MODEL slx_2e647110513d
CONFIG AbsTol = auto
CONFIG FixedStep = 0.001
CONFIG MaxStep = auto
CONFIG MinStep = auto
CONFIG RelTol = 1e-3
CONFIG SampleTimeConstraint = Unconstrained
CONFIG Solver = ode5
CONFIG SolverMode = Auto
CONFIG SolverName = ode5
CONFIG StartTime = 0.0
CONFIG StopTime = 15
BLOCK [SubSystem] Control Block
  Ports = [5, 1]
  RequestExecContextInheritance = off
BLOCK [Fcn] Control Block/Fcn
  Expr = cos(u)
BLOCK [Fcn] Control Block/Fcn1
  Expr = sin(u)/u
BLOCK [Gain] Control Block/Gain
  Gain = Kx
  OutDataTypeStr = Inherit: Inherit via internal rule
  ParamDataTypeStr = Inherit: Inherit via internal rule
  SaturateOnIntegerOverflow = off
BLOCK [Gain] Control Block/Gain1
  Gain = Ky
  OutDataTypeStr = Inherit: Inherit via internal rule
  ParamDataTypeStr = Inherit: Inherit via internal rule
  SaturateOnIntegerOverflow = off
BLOCK [Gain] Control Block/Gain2
  Gain = Kt
  OutDataTypeStr = Inherit: Inherit via internal rule
  ParamDataTypeStr = Inherit: Inherit via internal rule
  SaturateOnIntegerOverflow = off
BLOCK [Mux] Control Block/Mux
  DisplayOption = bar
  Inputs = 2
  Ports = [2, 1]
BLOCK [Mux] Control Block/Mux1
  DisplayOption = bar
  Inputs = 3
  Ports = [3, 1]
BLOCK [Product] Control Block/Product
  InputSameDT = off
  Inputs = 3
  OutDataTypeStr = Inherit: Inherit via internal rule
  Ports = [3, 1]
  RndMeth = Floor
  SaturateOnIntegerOverflow = off
BLOCK [Sum] Control Block/Sum3
  IconShape = round
  InputSameDT = off
  Inputs = |++
  OutDataTypeStr = Inherit: Inherit via internal rule
  Ports = [2, 1]
  SaturateOnIntegerOverflow = off
BLOCK [Sum] Control Block/Sum4
  IconShape = round
  InputSameDT = off
  Inputs = +++
  OutDataTypeStr = Inherit: Inherit via internal rule
  Ports = [3, 1]
  SaturateOnIntegerOverflow = off
BLOCK [ToWorkspace] Control Block/To Workspace
  FixptAsFi = on
  MaxDataPoints = inf
  Ports = [1]
  SampleTime = -1
  Save2DSignal = 3-D array (concatenate along third dimension)
  VariableName = error
BLOCK [Inport] Control Block/V_ref
  IconDisplay = Port number
  Port = 4
BLOCK [Inport] Control Block/theta_e
  IconDisplay = Port number
  Port = 3
BLOCK [Inport] Control Block/theta_ref
  IconDisplay = Port number
  Port = 5
BLOCK [Outport] Control Block/u_m
  IconDisplay = Port number
BLOCK [Inport] Control Block/x_e
  IconDisplay = Port number
BLOCK [Inport] Control Block/y_e
  IconDisplay = Port number
  Port = 2
BLOCK [SubSystem] DKM
  Ports = [1, 1]
  RequestExecContextInheritance = off
BLOCK [Constant] DKM/F_inv
  Value = [r/2 r/2; r/(2*L) -r/(2*L)]
BLOCK [ToWorkspace] DKM/To Workspace
  FixptAsFi = on
  MaxDataPoints = inf
  Ports = [1]
  SampleTime = -1
  Save2DSignal = 3-D array (concatenate along third dimension)
  VariableName = u
BLOCK [Inport] DKM/qm_dot
  IconDisplay = Port number
BLOCK [Outport] DKM/u_m 
  IconDisplay = Port number
BLOCK [Product] DKM/u_m Func
  InputSameDT = off
  Multiplication = Matrix(*)
  OutDataTypeStr = Inherit: Inherit via internal rule
  Ports = [2, 1]
  RndMeth = Floor
  SaturateOnIntegerOverflow = off
BLOCK [Gain] IKM
  Gain = [1/r_e L_e/r_e; 1/r_e  -L_e/r_e]
  Multiplication = Matrix(K*u) (u vector)
  OutDataTypeStr = Inherit: Inherit via internal rule
  ParamDataTypeStr = Inherit: Inherit via internal rule
  SaturateOnIntegerOverflow = off
BLOCK [SubSystem] Localization
  Ports = [1, 3]
  RequestExecContextInheritance = off
BLOCK [Demux] Localization/Demux
  DisplayOption = bar
  Outputs = 2
  Ports = [1, 2]
BLOCK [Fcn] Localization/Fcn
  Expr = cos(u)
BLOCK [Fcn] Localization/Fcn1
  Expr = sin(u)
BLOCK [Integrator] Localization/Integrator
  InitialCondition = theta0
  Ports = [1, 1]
BLOCK [Integrator] Localization/Integrator1
  InitialCondition = x0
  Ports = [1, 1]
BLOCK [Integrator] Localization/Integrator2
  InitialCondition = y0
  Ports = [1, 1]
BLOCK [Mux] Localization/Mux1
  DisplayOption = bar
  Inputs = 3
  Ports = [3, 1]
BLOCK [Product] Localization/Product
  InputSameDT = off
  OutDataTypeStr = Inherit: Inherit via internal rule
  Ports = [2, 1]
  RndMeth = Floor
  SaturateOnIntegerOverflow = off
BLOCK [Product] Localization/Product1
  InputSameDT = off
  OutDataTypeStr = Inherit: Inherit via internal rule
  Ports = [2, 1]
  RndMeth = Floor
  SaturateOnIntegerOverflow = off
BLOCK [ToWorkspace] Localization/To Workspace
  FixptAsFi = on
  MaxDataPoints = inf
  Ports = [1]
  SampleTime = -1
  Save2DSignal = 3-D array (concatenate along third dimension)
  VariableName = h
BLOCK [SubSystem] Localization/Transformation
  Ports = [3, 2]
  RequestExecContextInheritance = off
BLOCK [Inport] Localization/Transformation/0x
  IconDisplay = Port number
  Port = 2
BLOCK [Inport] Localization/Transformation/0y
  IconDisplay = Port number
  Port = 3
BLOCK [Demux] Localization/Transformation/Demux
  DisplayOption = bar
  Outputs = 2
  Ports = [1, 2]
BLOCK [Fcn] Localization/Transformation/Fcn2
  Expr = cos(u)
BLOCK [Fcn] Localization/Transformation/Fcn3
  Expr = sin(u)
BLOCK [Gain] Localization/Transformation/Gain
  Gain = -1
  OutDataTypeStr = Inherit: Inherit via internal rule
  ParamDataTypeStr = Inherit: Inherit via internal rule
  SaturateOnIntegerOverflow = off
BLOCK [Concatenate] Localization/Transformation/Matrix Concatenate
  ConcatenateDimension = 2
  Mode = Multidimensional array
  Ports = [2, 1]
BLOCK [Mux] Localization/Transformation/Mux1
  DisplayOption = bar
  Inputs = 2
  Ports = [2, 1]
BLOCK [Mux] Localization/Transformation/Mux2
  DisplayOption = bar
  Inputs = 2
  Ports = [2, 1]
BLOCK [Mux] Localization/Transformation/Mux3
  DisplayOption = bar
  Inputs = 2
  Ports = [2, 1]
BLOCK [Product] Localization/Transformation/Product
  InputSameDT = off
  Multiplication = Matrix(*)
  OutDataTypeStr = Inherit: Inherit via internal rule
  Ports = [2, 1]
  RndMeth = Floor
  SaturateOnIntegerOverflow = off
BLOCK [Outport] Localization/Transformation/mx
  IconDisplay = Port number
BLOCK [Outport] Localization/Transformation/my
  IconDisplay = Port number
  Port = 2
BLOCK [Inport] Localization/Transformation/theta
  IconDisplay = Port number
BLOCK [Outport] Localization/theta
  IconDisplay = Port number
  Port = 3
BLOCK [Inport] Localization/u_m
  IconDisplay = Port number
BLOCK [Outport] Localization/x
  IconDisplay = Port number
BLOCK [Outport] Localization/y
  IconDisplay = Port number
  Port = 2
BLOCK [Sum] Sum
  IconShape = round
  InputSameDT = off
  Inputs = -+|
  OutDataTypeStr = Inherit: Inherit via internal rule
  Ports = [2, 1]
  SaturateOnIntegerOverflow = off
BLOCK [Sum] Sum1
  IconShape = round
  InputSameDT = off
  Inputs = -+|
  OutDataTypeStr = Inherit: Inherit via internal rule
  Ports = [2, 1]
  SaturateOnIntegerOverflow = off
BLOCK [Sum] Sum2
  IconShape = round
  InputSameDT = off
  Inputs = -+|
  OutDataTypeStr = Inherit: Inherit via internal rule
  Ports = [2, 1]
  SaturateOnIntegerOverflow = off
BLOCK [SubSystem] Trajectory Generator
  Ports = [1, 5]
  RequestExecContextInheritance = off
BLOCK [Constant] Trajectory Generator/Constant
  Value = R
BLOCK [Constant] Trajectory Generator/Constant1
  Value = wd
BLOCK [Fcn] Trajectory Generator/Fcn
  Expr = u(1)*cos(u(2))
BLOCK [Fcn] Trajectory Generator/Fcn1
  Expr = u(1)*sin(u(2))
BLOCK [Fcn] Trajectory Generator/Fcn2
  Expr = u + pi/2
BLOCK [Integrator] Trajectory Generator/Integrator
  Ports = [1, 1]
BLOCK [Mux] Trajectory Generator/Mux
  DisplayOption = bar
  Inputs = 2
  Ports = [2, 1]
BLOCK [Mux] Trajectory Generator/Mux1
  DisplayOption = bar
  Inputs = 3
  Ports = [3, 1]
BLOCK [Product] Trajectory Generator/Product1
  InputSameDT = off
  OutDataTypeStr = Inherit: Inherit via internal rule
  Ports = [2, 1]
  RndMeth = Floor
  SaturateOnIntegerOverflow = off
BLOCK [ToWorkspace] Trajectory Generator/To Workspace
  FixptAsFi = on
  MaxDataPoints = inf
  Ports = [1]
  SampleTime = -1
  Save2DSignal = 3-D array (concatenate along third dimension)
  VariableName = hd
BLOCK [SubSystem] Trajectory Generator/Transformation
  Ports = [3, 2]
  RequestExecContextInheritance = off
BLOCK [Inport] Trajectory Generator/Transformation/0x
  IconDisplay = Port number
  Port = 2
BLOCK [Inport] Trajectory Generator/Transformation/0y
  IconDisplay = Port number
  Port = 3
BLOCK [Demux] Trajectory Generator/Transformation/Demux
  DisplayOption = bar
  Outputs = 2
  Ports = [1, 2]
BLOCK [Fcn] Trajectory Generator/Transformation/Fcn2
  Expr = cos(u)
BLOCK [Fcn] Trajectory Generator/Transformation/Fcn3
  Expr = sin(u)
BLOCK [Gain] Trajectory Generator/Transformation/Gain
  Gain = -1
  OutDataTypeStr = Inherit: Inherit via internal rule
  ParamDataTypeStr = Inherit: Inherit via internal rule
  SaturateOnIntegerOverflow = off
BLOCK [Concatenate] Trajectory Generator/Transformation/Matrix Concatenate
  ConcatenateDimension = 2
  Mode = Multidimensional array
  Ports = [2, 1]
BLOCK [Mux] Trajectory Generator/Transformation/Mux1
  DisplayOption = bar
  Inputs = 2
  Ports = [2, 1]
BLOCK [Mux] Trajectory Generator/Transformation/Mux2
  DisplayOption = bar
  Inputs = 2
  Ports = [2, 1]
BLOCK [Mux] Trajectory Generator/Transformation/Mux3
  DisplayOption = bar
  Inputs = 2
  Ports = [2, 1]
BLOCK [Product] Trajectory Generator/Transformation/Product
  InputSameDT = off
  Multiplication = Matrix(*)
  OutDataTypeStr = Inherit: Inherit via internal rule
  Ports = [2, 1]
  RndMeth = Floor
  SaturateOnIntegerOverflow = off
BLOCK [Outport] Trajectory Generator/Transformation/mx
  IconDisplay = Port number
BLOCK [Outport] Trajectory Generator/Transformation/my
  IconDisplay = Port number
  Port = 2
BLOCK [Inport] Trajectory Generator/Transformation/theta
  IconDisplay = Port number
BLOCK [Outport] Trajectory Generator/Vd
  IconDisplay = Port number
  Port = 4
BLOCK [Inport] Trajectory Generator/theta
  IconDisplay = Port number
BLOCK [Outport] Trajectory Generator/thetad
  IconDisplay = Port number
  Port = 3
BLOCK [Outport] Trajectory Generator/wd
  IconDisplay = Port number
  Port = 5
BLOCK [Outport] Trajectory Generator/xd
  IconDisplay = Port number
BLOCK [Outport] Trajectory Generator/yd
  IconDisplay = Port number
  Port = 2
LINE Control Block/Fcn1:1 -> Control Block/Product:3
LINE Control Block/Fcn:1 -> Control Block/Sum3:2
LINE Control Block/Gain1:1 -> Control Block/Product:1
LINE Control Block/Gain2:1 -> Control Block/Sum4:2
LINE Control Block/Gain:1 -> Control Block/Sum3:1
LINE Control Block/Mux1:1 -> Control Block/To Workspace:1
LINE Control Block/Mux:1 -> Control Block/u_m:1
LINE Control Block/Product:1 -> Control Block/Sum4:1
LINE Control Block/Sum3:1 -> Control Block/Mux:1
LINE Control Block/Sum4:1 -> Control Block/Mux:2
LINE Control Block/V_ref:1 -> Control Block/Product:2
LINE Control Block/theta_e:1 -> Control Block/Fcn1:1
LINE Control Block/theta_e:1 -> Control Block/Fcn:1
LINE Control Block/theta_e:1 -> Control Block/Gain2:1
LINE Control Block/theta_e:1 -> Control Block/Mux1:3
LINE Control Block/theta_ref:1 -> Control Block/Sum4:3
LINE Control Block/x_e:1 -> Control Block/Gain:1
LINE Control Block/x_e:1 -> Control Block/Mux1:1
LINE Control Block/y_e:1 -> Control Block/Gain1:1
LINE Control Block/y_e:1 -> Control Block/Mux1:2
LINE Control Block:1 -> IKM:1
LINE DKM/F_inv:1 -> DKM/u_m Func:1
LINE DKM/qm_dot:1 -> DKM/u_m Func:2
LINE DKM/u_m Func:1 -> DKM/To Workspace:1
LINE DKM/u_m Func:1 -> DKM/u_m :1
LINE DKM:1 -> Localization:1
LINE IKM:1 -> DKM:1
LINE Localization/Demux:1 -> Localization/Product1:1
LINE Localization/Demux:1 -> Localization/Product:1
LINE Localization/Demux:2 -> Localization/Integrator:1
LINE Localization/Fcn1:1 -> Localization/Product1:2
LINE Localization/Fcn:1 -> Localization/Product:2
LINE Localization/Integrator1:1 -> Localization/Mux1:1
LINE Localization/Integrator1:1 -> Localization/Transformation:2
LINE Localization/Integrator2:1 -> Localization/Mux1:2
LINE Localization/Integrator2:1 -> Localization/Transformation:3
LINE Localization/Integrator:1 -> Localization/Fcn1:1
LINE Localization/Integrator:1 -> Localization/Fcn:1
LINE Localization/Integrator:1 -> Localization/Mux1:3
LINE Localization/Integrator:1 -> Localization/Transformation:1
LINE Localization/Integrator:1 -> Localization/theta:1
LINE Localization/Mux1:1 -> Localization/To Workspace:1
LINE Localization/Product1:1 -> Localization/Integrator2:1
LINE Localization/Product:1 -> Localization/Integrator1:1
LINE Localization/Transformation/0x:1 -> Localization/Transformation/Mux1:1
LINE Localization/Transformation/0y:1 -> Localization/Transformation/Mux1:2
LINE Localization/Transformation/Demux:1 -> Localization/Transformation/mx:1
LINE Localization/Transformation/Demux:2 -> Localization/Transformation/my:1
LINE Localization/Transformation/Fcn2:1 -> Localization/Transformation/Mux2:1
LINE Localization/Transformation/Fcn2:1 -> Localization/Transformation/Mux3:2
LINE Localization/Transformation/Fcn3:1 -> Localization/Transformation/Gain:1
LINE Localization/Transformation/Fcn3:1 -> Localization/Transformation/Mux3:1
LINE Localization/Transformation/Gain:1 -> Localization/Transformation/Mux2:2
LINE Localization/Transformation/Matrix Concatenate:1 -> Localization/Transformation/Product:1
LINE Localization/Transformation/Mux1:1 -> Localization/Transformation/Product:2
LINE Localization/Transformation/Mux2:1 -> Localization/Transformation/Matrix Concatenate:1
LINE Localization/Transformation/Mux3:1 -> Localization/Transformation/Matrix Concatenate:2
LINE Localization/Transformation/Product:1 -> Localization/Transformation/Demux:1
LINE Localization/Transformation/theta:1 -> Localization/Transformation/Fcn2:1
LINE Localization/Transformation/theta:1 -> Localization/Transformation/Fcn3:1
LINE Localization/Transformation:1 -> Localization/x:1
LINE Localization/Transformation:2 -> Localization/y:1
LINE Localization/u_m:1 -> Localization/Demux:1
LINE Localization:1 -> Sum:1
LINE Localization:2 -> Sum1:1
LINE Localization:3 -> Sum2:1
LINE Localization:3 -> Trajectory Generator:1
LINE Sum1:1 -> Control Block:2
LINE Sum2:1 -> Control Block:3
LINE Sum:1 -> Control Block:1
LINE Trajectory Generator/Constant1:1 -> Trajectory Generator/Integrator:1
LINE Trajectory Generator/Constant1:1 -> Trajectory Generator/Product1:2
LINE Trajectory Generator/Constant1:1 -> Trajectory Generator/wd:1
LINE Trajectory Generator/Constant:1 -> Trajectory Generator/Mux:1
LINE Trajectory Generator/Constant:1 -> Trajectory Generator/Product1:1
LINE Trajectory Generator/Fcn1:1 -> Trajectory Generator/Mux1:2
LINE Trajectory Generator/Fcn1:1 -> Trajectory Generator/Transformation:3
LINE Trajectory Generator/Fcn2:1 -> Trajectory Generator/Mux1:3
LINE Trajectory Generator/Fcn2:1 -> Trajectory Generator/thetad:1
LINE Trajectory Generator/Fcn:1 -> Trajectory Generator/Mux1:1
LINE Trajectory Generator/Fcn:1 -> Trajectory Generator/Transformation:2
LINE Trajectory Generator/Integrator:1 -> Trajectory Generator/Fcn2:1
LINE Trajectory Generator/Integrator:1 -> Trajectory Generator/Mux:2
LINE Trajectory Generator/Mux1:1 -> Trajectory Generator/To Workspace:1
LINE Trajectory Generator/Mux:1 -> Trajectory Generator/Fcn1:1
LINE Trajectory Generator/Mux:1 -> Trajectory Generator/Fcn:1
LINE Trajectory Generator/Product1:1 -> Trajectory Generator/Vd:1
LINE Trajectory Generator/Transformation/0x:1 -> Trajectory Generator/Transformation/Mux1:1
LINE Trajectory Generator/Transformation/0y:1 -> Trajectory Generator/Transformation/Mux1:2
LINE Trajectory Generator/Transformation/Demux:1 -> Trajectory Generator/Transformation/mx:1
LINE Trajectory Generator/Transformation/Demux:2 -> Trajectory Generator/Transformation/my:1
LINE Trajectory Generator/Transformation/Fcn2:1 -> Trajectory Generator/Transformation/Mux2:1
LINE Trajectory Generator/Transformation/Fcn2:1 -> Trajectory Generator/Transformation/Mux3:2
LINE Trajectory Generator/Transformation/Fcn3:1 -> Trajectory Generator/Transformation/Gain:1
LINE Trajectory Generator/Transformation/Fcn3:1 -> Trajectory Generator/Transformation/Mux3:1
LINE Trajectory Generator/Transformation/Gain:1 -> Trajectory Generator/Transformation/Mux2:2
LINE Trajectory Generator/Transformation/Matrix Concatenate:1 -> Trajectory Generator/Transformation/Product:1
LINE Trajectory Generator/Transformation/Mux1:1 -> Trajectory Generator/Transformation/Product:2
LINE Trajectory Generator/Transformation/Mux2:1 -> Trajectory Generator/Transformation/Matrix Concatenate:1
LINE Trajectory Generator/Transformation/Mux3:1 -> Trajectory Generator/Transformation/Matrix Concatenate:2
LINE Trajectory Generator/Transformation/Product:1 -> Trajectory Generator/Transformation/Demux:1
LINE Trajectory Generator/Transformation/theta:1 -> Trajectory Generator/Transformation/Fcn2:1
LINE Trajectory Generator/Transformation/theta:1 -> Trajectory Generator/Transformation/Fcn3:1
LINE Trajectory Generator/Transformation:1 -> Trajectory Generator/xd:1
LINE Trajectory Generator/Transformation:2 -> Trajectory Generator/yd:1
LINE Trajectory Generator/theta:1 -> Trajectory Generator/Transformation:1
LINE Trajectory Generator:1 -> Sum:2
LINE Trajectory Generator:2 -> Sum1:2
LINE Trajectory Generator:3 -> Sum2:2
LINE Trajectory Generator:4 -> Control Block:4
LINE Trajectory Generator:5 -> Control Block:5
